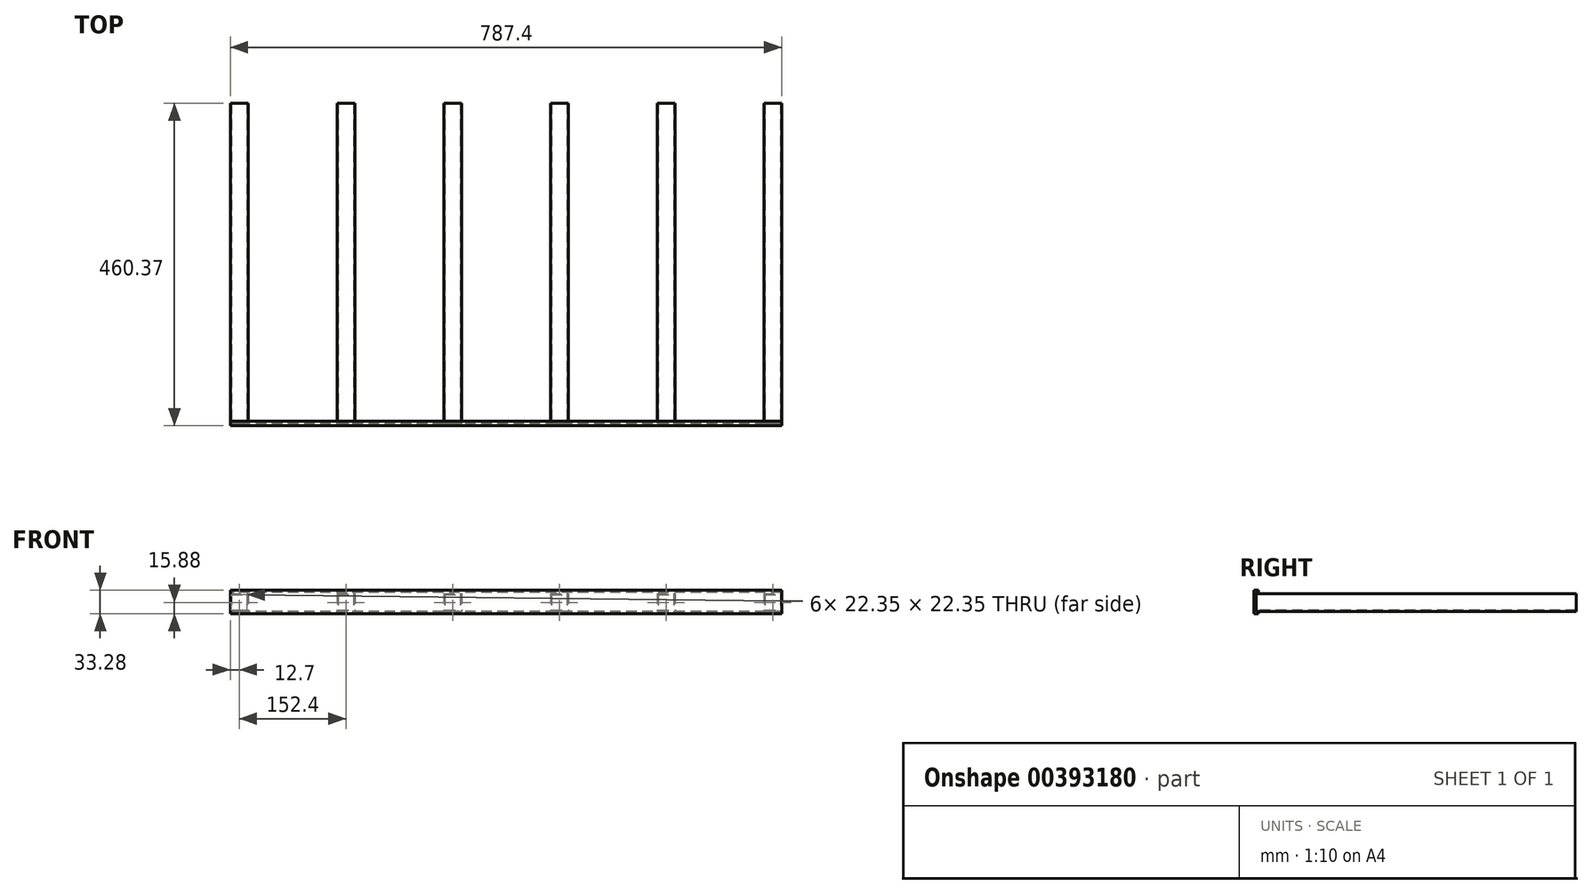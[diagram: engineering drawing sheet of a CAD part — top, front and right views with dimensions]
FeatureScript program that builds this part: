
annotation { "Feature Type Name" : "Feature", "Feature Type Description" : "" }
export const myFeature = defineFeature(function(context is Context, id is Id, definition is map)
    precondition{}
    {
        {
            var Q0;
            Q0=qCreatedBy(makeId("Front.planeOp"),FACE);
            var sketch = newSketch(context, id + "F0", { "sketchPlane" : qUnion([Q0])});
            skLineSegment(sketch, "E0.bottom", {"start": v(0, 0) * mm, "end": v(25.4, 0) * mm});
            skLineSegment(sketch, "E0.top", {"start": v(0, -25.4) * mm, "end": v(25.4, -25.4) * mm});
            skLineSegment(sketch, "E0.left", {"start": v(0, 0) * mm, "end": v(0, -25.4) * mm});
            skLineSegment(sketch, "E0.right", {"start": v(25.4, 0) * mm, "end": v(25.4, -25.4) * mm});
            skLineSegment(sketch, "E1.0", {"start": v(1.52, -1.52) * mm, "end": v(1.52, -23.88) * mm});
            skLineSegment(sketch, "E2.0", {"start": v(1.52, -1.52) * mm, "end": v(23.88, -1.52) * mm});
            skLineSegment(sketch, "E3.0", {"start": v(23.88, -1.52) * mm, "end": v(23.88, -23.88) * mm});
            skLineSegment(sketch, "E4.0", {"start": v(1.52, -23.88) * mm, "end": v(23.88, -23.88) * mm});
            skLineSegment(sketch, "E5.1.0.0", {"start": v(153.92, -1.52) * mm, "end": v(176.28, -1.52) * mm});
            skLineSegment(sketch, "E5.1.0.1", {"start": v(153.92, -1.52) * mm, "end": v(153.92, -23.88) * mm});
            skLineSegment(sketch, "E5.1.0.2", {"start": v(177.8, 0) * mm, "end": v(177.8, -25.4) * mm});
            skLineSegment(sketch, "E5.1.0.3", {"start": v(176.28, -1.52) * mm, "end": v(176.28, -23.88) * mm});
            skLineSegment(sketch, "E5.1.0.4", {"start": v(153.92, -23.88) * mm, "end": v(176.28, -23.88) * mm});
            skLineSegment(sketch, "E5.1.0.5", {"start": v(152.4, 0) * mm, "end": v(152.4, -25.4) * mm});
            skLineSegment(sketch, "E5.1.0.6", {"start": v(152.4, -25.4) * mm, "end": v(177.8, -25.4) * mm});
            skLineSegment(sketch, "E5.1.0.7", {"start": v(152.4, 0) * mm, "end": v(177.8, 0) * mm});
            skLineSegment(sketch, "E5.2.0.0", {"start": v(306.32, -1.52) * mm, "end": v(328.68, -1.52) * mm});
            skLineSegment(sketch, "E5.2.0.1", {"start": v(306.32, -1.52) * mm, "end": v(306.32, -23.88) * mm});
            skLineSegment(sketch, "E5.2.0.2", {"start": v(330.2, 0) * mm, "end": v(330.2, -25.4) * mm});
            skLineSegment(sketch, "E5.2.0.3", {"start": v(328.68, -1.52) * mm, "end": v(328.68, -23.88) * mm});
            skLineSegment(sketch, "E5.2.0.4", {"start": v(306.32, -23.88) * mm, "end": v(328.68, -23.88) * mm});
            skLineSegment(sketch, "E5.2.0.5", {"start": v(304.8, 0) * mm, "end": v(304.8, -25.4) * mm});
            skLineSegment(sketch, "E5.2.0.6", {"start": v(304.8, -25.4) * mm, "end": v(330.2, -25.4) * mm});
            skLineSegment(sketch, "E5.2.0.7", {"start": v(304.8, 0) * mm, "end": v(330.2, 0) * mm});
            skLineSegment(sketch, "E5.3.0.0", {"start": v(458.72, -1.52) * mm, "end": v(481.08, -1.52) * mm});
            skLineSegment(sketch, "E5.3.0.1", {"start": v(458.72, -1.52) * mm, "end": v(458.72, -23.88) * mm});
            skLineSegment(sketch, "E5.3.0.2", {"start": v(482.6, 0) * mm, "end": v(482.6, -25.4) * mm});
            skLineSegment(sketch, "E5.3.0.3", {"start": v(481.08, -1.52) * mm, "end": v(481.08, -23.88) * mm});
            skLineSegment(sketch, "E5.3.0.4", {"start": v(458.72, -23.88) * mm, "end": v(481.08, -23.88) * mm});
            skLineSegment(sketch, "E5.3.0.5", {"start": v(457.2, 0) * mm, "end": v(457.2, -25.4) * mm});
            skLineSegment(sketch, "E5.3.0.6", {"start": v(457.2, -25.4) * mm, "end": v(482.6, -25.4) * mm});
            skLineSegment(sketch, "E5.3.0.7", {"start": v(457.2, 0) * mm, "end": v(482.6, 0) * mm});
            skLineSegment(sketch, "E5.4.0.0", {"start": v(611.12, -1.52) * mm, "end": v(633.48, -1.52) * mm});
            skLineSegment(sketch, "E5.4.0.1", {"start": v(611.12, -1.52) * mm, "end": v(611.12, -23.88) * mm});
            skLineSegment(sketch, "E5.4.0.2", {"start": v(635, 0) * mm, "end": v(635, -25.4) * mm});
            skLineSegment(sketch, "E5.4.0.3", {"start": v(633.48, -1.52) * mm, "end": v(633.48, -23.88) * mm});
            skLineSegment(sketch, "E5.4.0.4", {"start": v(611.12, -23.88) * mm, "end": v(633.48, -23.88) * mm});
            skLineSegment(sketch, "E5.4.0.5", {"start": v(609.6, 0) * mm, "end": v(609.6, -25.4) * mm});
            skLineSegment(sketch, "E5.4.0.6", {"start": v(609.6, -25.4) * mm, "end": v(635, -25.4) * mm});
            skLineSegment(sketch, "E5.4.0.7", {"start": v(609.6, 0) * mm, "end": v(635, 0) * mm});
            skLineSegment(sketch, "E5.5.0.0", {"start": v(763.52, -1.52) * mm, "end": v(785.88, -1.52) * mm});
            skLineSegment(sketch, "E5.5.0.1", {"start": v(763.52, -1.52) * mm, "end": v(763.52, -23.88) * mm});
            skLineSegment(sketch, "E5.5.0.2", {"start": v(787.4, 0) * mm, "end": v(787.4, -25.4) * mm});
            skLineSegment(sketch, "E5.5.0.3", {"start": v(785.88, -1.52) * mm, "end": v(785.88, -23.88) * mm});
            skLineSegment(sketch, "E5.5.0.4", {"start": v(763.52, -23.88) * mm, "end": v(785.88, -23.88) * mm});
            skLineSegment(sketch, "E5.5.0.5", {"start": v(762, 0) * mm, "end": v(762, -25.4) * mm});
            skLineSegment(sketch, "E5.5.0.6", {"start": v(762, -25.4) * mm, "end": v(787.4, -25.4) * mm});
            skLineSegment(sketch, "E5.5.0.7", {"start": v(762, 0) * mm, "end": v(787.4, 0) * mm});
            skLineSegment(sketch, "E5.direction1", {"start": v(0, -25.4) * mm, "end": v(152.4, -25.4) * mm, "construction": true});
            skSolve(sketch);
        }
        {
            var Q0;
            Q0 = qSketchRegion(id + "F0", true);
            extrude(context, id + "F1", {"entities" : qUnion([Q0]), "oppositeDirection" : true, "depth" : 457.2 * mm});
        }
        {
            var Q0;
            Q0=qCreatedBy(makeId("Right.planeOp"),FACE);
            var sketch = newSketch(context, id + "F2", { "sketchPlane" : qUnion([Q0])});
            skLineSegment(sketch, "E6", {"start": v(3.17, 4.7) * mm, "end": v(-3.18, 4.7) * mm});
            skLineSegment(sketch, "E7", {"start": v(-3.18, 4.7) * mm, "end": v(-3.17, -28.58) * mm});
            skLineSegment(sketch, "E8", {"start": v(-3.17, -28.58) * mm, "end": v(3.18, -28.58) * mm});
            skLineSegment(sketch, "E9", {"start": v(3.18, -28.58) * mm, "end": v(3.18, -25.4) * mm});
            skLineSegment(sketch, "E10", {"start": v(3.18, -25.4) * mm, "end": v(0, -25.4) * mm});
            skLineSegment(sketch, "E11", {"start": v(3.17, 4.7) * mm, "end": v(3.17, 1.52) * mm});
            skLineSegment(sketch, "E12", {"start": v(3.17, 1.52) * mm, "end": v(0, 1.52) * mm});
            skLineSegment(sketch, "E13", {"start": v(0, 1.52) * mm, "end": v(0, -25.4) * mm});
            skSolve(sketch);
        }
        {
            var Q0;
            Q0=makeQuery(id+"F2.imprint","IMPRINT",FACE,{"disambiguationData":[TD([[makeQuery(id+"F2.imprint","IMPRINT",EDGE,{"derivedFrom":sQuery(id+"F2.wireOp",EDGE,"E6")}),1.0]])]});
            extrude(context, id + "F3", {"entities" : qUnion([Q0]), "depth" : 787.4 * mm});
        }
    });
